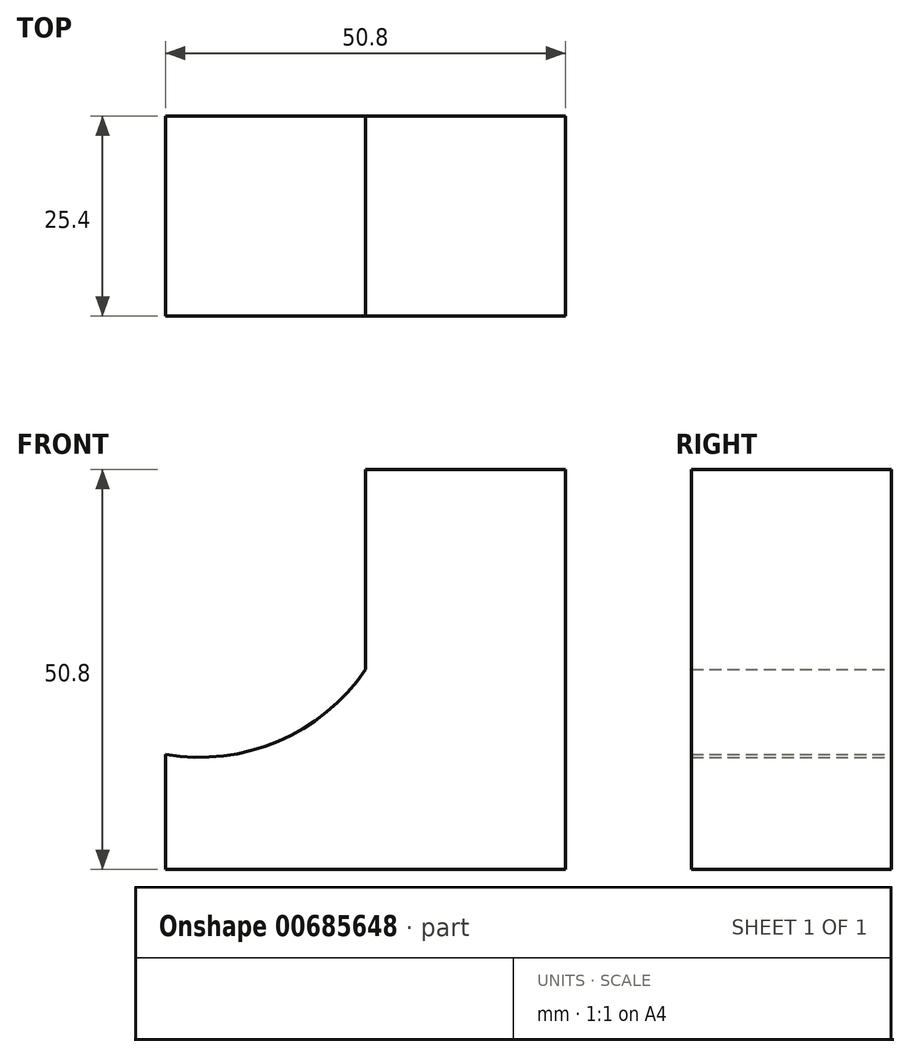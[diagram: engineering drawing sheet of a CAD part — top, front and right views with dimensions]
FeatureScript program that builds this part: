
annotation { "Feature Type Name" : "Feature", "Feature Type Description" : "" }
export const myFeature = defineFeature(function(context is Context, id is Id, definition is map)
    precondition{}
    {
        {
            var Q0;
            Q0=qCreatedBy(makeId("Front.planeOp"),FACE);
            var sketch = newSketch(context, id + "F0", { "sketchPlane" : qUnion([Q0])});
            skLineSegment(sketch, "E0", {"start": v(0, 0) * mm, "end": v(-50.8, 0) * mm});
            skLineSegment(sketch, "E1", {"start": v(0, 0) * mm, "end": v(0, 50.8) * mm});
            skLineSegment(sketch, "E2", {"start": v(0, 50.8) * mm, "end": v(-25.4, 50.8) * mm});
            skLineSegment(sketch, "E3", {"start": v(-50.8, 0) * mm, "end": v(-50.8, 14.62) * mm});
            skLineSegment(sketch, "E4", {"start": v(-25.4, 50.8) * mm, "end": v(-25.4, 25.4) * mm});
            skArc(sketch, "E5", {"start": v(-50.8, 14.62) * mm, "mid": v(-36.5, 16.26) * mm, "end": v(-25.4, 25.4) * mm});
            skSolve(sketch);
        }
        {
            var Q0;
            Q0 = qSketchRegion(id + "F0", true);
            extrude(context, id + "F1", {"entities" : qUnion([Q0]), "depth" : 25.4 * mm, "offsetDistance" : 25.4 * mm});
        }
    });
